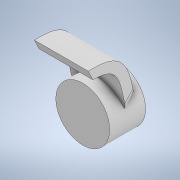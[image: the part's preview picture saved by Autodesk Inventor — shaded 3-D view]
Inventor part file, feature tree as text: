
AUTODESK INVENTOR PART (.ipt)
format: ipt  version: 2021 (Build 250183000, 183)  size: 153,088 bytes
history: native  units: mm
features: sketch x3, extrude x1, sweep x1, fillet x1
ambient origin geometry x8: Origin, YZ Plane, XZ Plane, XY Plane, X Axis, Y Axis, Z Axis, Center Point
bodies: Solid1 (feature_tree)
feature tree (6):
  extrude  "Extrusion1"  Depth=10.0mm TaperAngle=0.0deg
  sweep  "Sweep1"
  fillet  "Fillet1"  Radius=3.0mm
  sketch  "Sketch1"  dims[d0=15.0mm d1=10.0mm d2=0.0mm]
  sketch  "Sketch2"  dims[d3=15.0mm d4=15.0mm d5=3.0mm]
  sketch  "Sketch3"  dims[d6=0.0mm d7=0.0mm d8=2.0mm]
